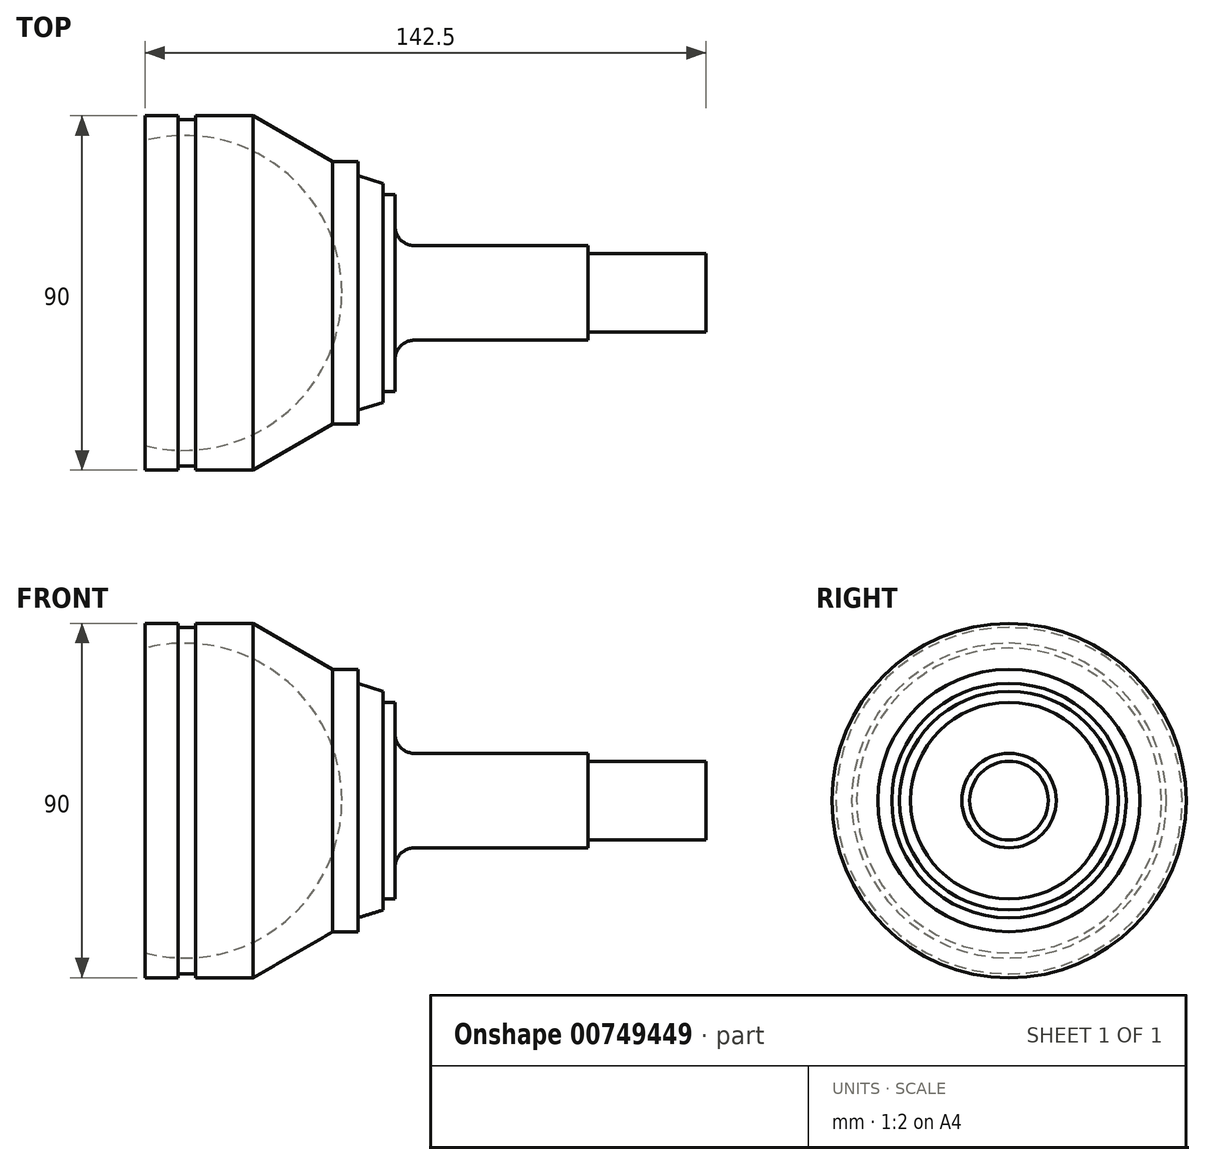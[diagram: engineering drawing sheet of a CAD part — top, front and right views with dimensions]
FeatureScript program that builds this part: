
annotation { "Feature Type Name" : "Feature", "Feature Type Description" : "" }
export const myFeature = defineFeature(function(context is Context, id is Id, definition is map)
    precondition{}
    {
        {
            var Q0;
            Q0=qCreatedBy(makeId("Front.planeOp"),FACE);
            var sketch = newSketch(context, id + "F0", { "sketchPlane" : qUnion([Q0])});
            skLineSegment(sketch, "E0", {"start": v(0, 45) * mm, "end": v(8.4, 45) * mm});
            skLineSegment(sketch, "E1", {"start": v(8.4, 45) * mm, "end": v(8.4, 44) * mm});
            skLineSegment(sketch, "E2", {"start": v(8.4, 44) * mm, "end": v(12.84, 44) * mm});
            skLineSegment(sketch, "E3", {"start": v(12.84, 44) * mm, "end": v(12.84, 45) * mm});
            skLineSegment(sketch, "E4", {"start": v(12.84, 45) * mm, "end": v(27.45, 45) * mm});
            skLineSegment(sketch, "E5", {"start": v(27.45, 45) * mm, "end": v(47.69, 33.31) * mm});
            skLineSegment(sketch, "E6", {"start": v(47.69, 33.31) * mm, "end": v(54.15, 33.31) * mm});
            skLineSegment(sketch, "E7", {"start": v(54.15, 33.31) * mm, "end": v(54.15, 29.77) * mm});
            skLineSegment(sketch, "E8", {"start": v(54.15, 29.77) * mm, "end": v(60.44, 27.8) * mm});
            skLineSegment(sketch, "E9", {"start": v(60.44, 27.8) * mm, "end": v(60.44, 25) * mm});
            skLineSegment(sketch, "E10", {"start": v(60.44, 25) * mm, "end": v(63.5, 25) * mm});
            skLineSegment(sketch, "E11", {"start": v(63.5, 25) * mm, "end": v(63.5, 12) * mm});
            skLineSegment(sketch, "E12", {"start": v(63.5, 12) * mm, "end": v(112.5, 12) * mm});
            skLineSegment(sketch, "E13", {"start": v(112.5, 12) * mm, "end": v(112.5, 10) * mm});
            skLineSegment(sketch, "E14", {"start": v(112.5, 10) * mm, "end": v(142.5, 10) * mm});
            skLineSegment(sketch, "E15", {"start": v(142.5, 10) * mm, "end": v(142.5, 0) * mm});
            skLineSegment(sketch, "E16", {"start": v(142.5, 0) * mm, "end": v(50, 0) * mm});
            skLineSegment(sketch, "E17", {"start": v(0, 45) * mm, "end": v(0, 38.73) * mm});
            skArc(sketch, "E18", {"start": v(50, 0) * mm, "mid": v(34.5, 31.62) * mm, "end": v(0, 38.73) * mm});
            skSolve(sketch);
        }
        {
            var Q0;
            Q0=makeQuery(id+"F0.imprint","IMPRINT",FACE,{"disambiguationData":[TD([[makeQuery(id+"F0.imprint","IMPRINT",EDGE,{"derivedFrom":sQuery(id+"F0.wireOp",EDGE,"E0")}),-1.0]])]});
            var Q1;
            Q1=sQuery(id+"F0.wireOp",EDGE,"E16");
            revolve(context, id + "F1", {"surfaceOperationType" : NewSurfaceOperationType.NEW, "entities" : qUnion([Q0]), "axis" : qUnion([Q1]), "revolveType" : RevolveType.FULL});
        }
        {
            var Q0;
            Q0=makeQuery(id+"F1.opRevolve","SWEPT_EDGE",EDGE,{"disambiguationData":[OSD([sQuery(id+"F0.wireOp",EDGE,"E11"),sQuery(id+"F0.wireOp",EDGE,"E12")])]});
            fillet(context, id + "F2", {"entities" : qUnion([Q0]), "radius" : 5 * mm, "tangentPropagation" : true, "allowEdgeOverflow" : false});
        }
    });
